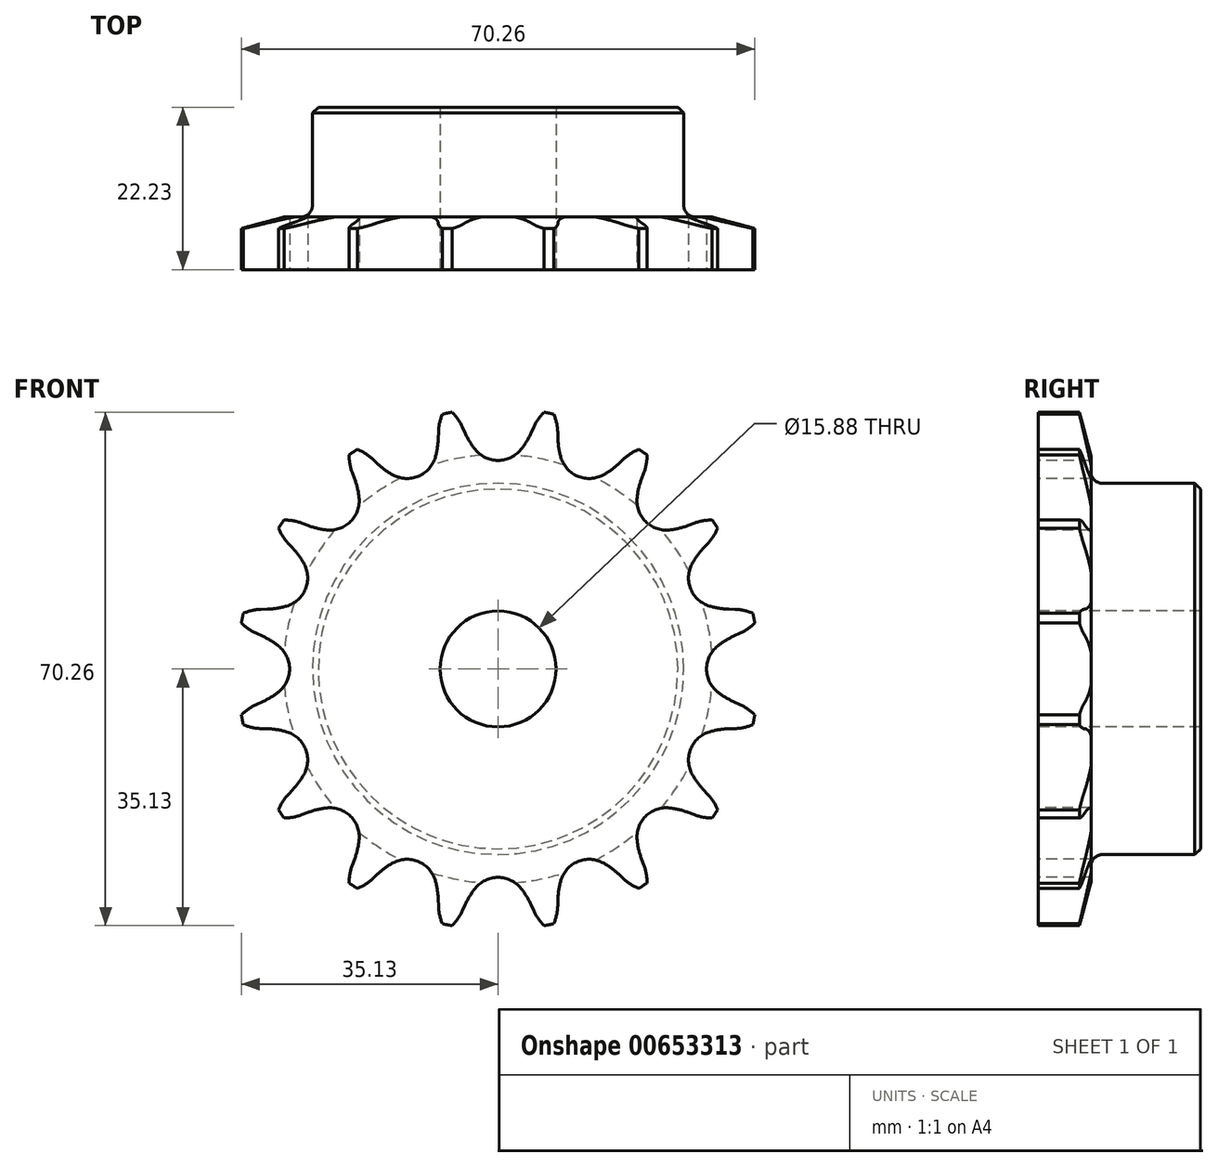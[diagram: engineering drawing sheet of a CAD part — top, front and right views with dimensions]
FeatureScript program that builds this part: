
annotation { "Feature Type Name" : "Feature", "Feature Type Description" : "" }
export const myFeature = defineFeature(function(context is Context, id is Id, definition is map)
    precondition{}
    {
        {
            var Q0;
            Q0=qCreatedBy(makeId("Right.planeOp"),FACE);
            var sketch = newSketch(context, id + "F0", { "sketchPlane" : qUnion([Q0])});
            skLineSegment(sketch, "E0", {"start": v(0, 0) * mm, "end": v(22.22, 0) * mm, "construction": true});
            skLineSegment(sketch, "E1", {"start": v(0, 35.69) * mm, "end": v(7.21, 35.69) * mm});
            skLineSegment(sketch, "E2", {"start": v(7.21, 35.69) * mm, "end": v(7.21, 25.4) * mm});
            skLineSegment(sketch, "E3", {"start": v(7.21, 25.4) * mm, "end": v(22.23, 25.4) * mm});
            skLineSegment(sketch, "E4", {"start": v(22.22, 25.4) * mm, "end": v(22.22, 7.94) * mm});
            skLineSegment(sketch, "E5", {"start": v(22.23, 7.94) * mm, "end": v(0, 7.94) * mm});
            skLineSegment(sketch, "E6", {"start": v(0, 7.94) * mm, "end": v(0, 35.69) * mm});
            skLineSegment(sketch, "E7.0.MirrorCS", {"start": v(0, -35.69) * mm, "end": v(7.21, -35.69) * mm});
            skLineSegment(sketch, "E7.1.MirrorCS", {"start": v(7.21, -35.69) * mm, "end": v(7.21, -25.4) * mm});
            skLineSegment(sketch, "E7.2.MirrorCS", {"start": v(22.23, -7.94) * mm, "end": v(0, -7.94) * mm});
            skLineSegment(sketch, "E7.3.MirrorCS", {"start": v(22.23, -25.4) * mm, "end": v(22.23, -7.94) * mm});
            skLineSegment(sketch, "E7.4.MirrorCS", {"start": v(7.21, -25.4) * mm, "end": v(22.23, -25.4) * mm});
            skLineSegment(sketch, "E7.5.MirrorCS", {"start": v(0, -7.94) * mm, "end": v(0, -35.69) * mm});
            skSolve(sketch);
        }
        {
            var Q0;
            Q0=makeQuery(id+"F0.imprint","IMPRINT",FACE,{"disambiguationData":[TD([[makeQuery(id+"F0.imprint","IMPRINT",EDGE,{"derivedFrom":sQuery(id+"F0.wireOp",EDGE,"E1")}),-1.0]])]});
            var Q1;
            Q1=sQuery(id+"F0.wireOp",EDGE,"E0");
            revolve(context, id + "F1", {"entities" : qUnion([Q0]), "axis" : qUnion([Q1]), "revolveType" : RevolveType.FULL});
        }
        {
            var Q0;
            Q0=makeQuery(id+"F1.opRevolve","SWEPT_EDGE",EDGE,{"disambiguationData":[OSD([sQuery(id+"F0.wireOp",EDGE,"E1"),sQuery(id+"F0.wireOp",EDGE,"E2")])]});
            chamfer(context, id + "F2", {"entities" : qUnion([Q0]), "chamferType" : ChamferType.TWO_OFFSETS, "width1" : 6.35 * mm, "oppositeDirection" : true, "width2" : 1.57 * mm, "tangentPropagation" : true});
        }
        {
            var Q0;
            Q0=makeQuery(id+"F1.opRevolve","SWEPT_FACE",FACE,{"disambiguationData":[OSD([sQuery(id+"F0.wireOp",EDGE,"E6")])]});
            var sketch = newSketch(context, id + "F3", { "sketchPlane" : qUnion([Q0])});
            skCircle(sketch, "E8", {"center": v(0, 0) * mm, "radius": 32.55 * mm, "construction": true});
            skLineSegment(sketch, "E9", {"start": v(0, 0) * mm, "end": v(0, 32.55) * mm, "construction": true});
            skLineSegment(sketch, "E10", {"start": v(0, 32.55) * mm, "end": v(25.8, 32.55) * mm, "construction": true});
            skPoint(sketch, "E11", {"position": v(-10.88, 30.38) * mm});
            skPoint(sketch, "E12", {"position": v(4.95, 36.52) * mm});
            skLineSegment(sketch, "E13", {"start": v(0, 32.55) * mm, "end": v(4.95, 36.52) * mm, "construction": true});
            skLineSegment(sketch, "E14", {"start": v(4.95, 36.52) * mm, "end": v(-4.5, 32.26) * mm, "construction": true});
            skLineSegment(sketch, "E15", {"start": v(-4.5, 32.26) * mm, "end": v(-4.88, 33.1) * mm});
            skLineSegment(sketch, "E16", {"start": v(0, 0) * mm, "end": v(-7.12, 35.8) * mm, "construction": true});
            skArc(sketch, "E17", {"start": v(-7.12, 35.8) * mm, "mid": v(-15.95, 26.17) * mm, "end": v(-4.88, 33.1) * mm, "construction": true});
            skArc(sketch, "E18", {"start": v(-4.88, 33.1) * mm, "mid": v(-5.81, 34.6) * mm, "end": v(-7.12, 35.8) * mm});
            skArc(sketch, "E19", {"start": v(-3.14, 30.03) * mm, "mid": v(13.78, 41.93) * mm, "end": v(-4.5, 32.26) * mm, "construction": true});
            skArc(sketch, "E20", {"start": v(-4.5, 32.26) * mm, "mid": v(-3.89, 31.1) * mm, "end": v(-3.14, 30.03) * mm});
            skLineSegment(sketch, "E21", {"start": v(4.4, 12.5) * mm, "end": v(-4.88, 33.1) * mm, "construction": true});
            skArc(sketch, "E22.0.MirrorCS", {"start": v(4.5, 32.26) * mm, "mid": v(3.89, 31.1) * mm, "end": v(3.14, 30.03) * mm});
            skLineSegment(sketch, "E23.0.MirrorCS", {"start": v(4.5, 32.26) * mm, "end": v(4.88, 33.1) * mm});
            skArc(sketch, "E24.0.MirrorCS", {"start": v(4.88, 33.1) * mm, "mid": v(5.81, 34.6) * mm, "end": v(7.12, 35.8) * mm});
            skArc(sketch, "E25", {"start": v(-3.14, 30.03) * mm, "mid": v(0, 28.53) * mm, "end": v(3.14, 30.03) * mm});
            skArc(sketch, "E26", {"start": v(3.14, 30.03) * mm, "mid": v(0, 36.57) * mm, "end": v(-3.14, 30.03) * mm, "construction": true});
            skArc(sketch, "E27.1.0", {"start": v(-17.17, 28.7) * mm, "mid": v(-18.61, 29.74) * mm, "end": v(-20.28, 30.34) * mm});
            skLineSegment(sketch, "E27.1.1", {"start": v(-16.5, 28.08) * mm, "end": v(-17.17, 28.7) * mm});
            skArc(sketch, "E27.1.2", {"start": v(-16.5, 28.08) * mm, "mid": v(-15.5, 27.25) * mm, "end": v(-14.39, 26.55) * mm});
            skArc(sketch, "E27.1.3", {"start": v(-14.39, 26.55) * mm, "mid": v(-10.92, 26.36) * mm, "end": v(-8.6, 28.95) * mm});
            skArc(sketch, "E27.1.4", {"start": v(-8.19, 31.53) * mm, "mid": v(-8.3, 30.22) * mm, "end": v(-8.6, 28.95) * mm});
            skLineSegment(sketch, "E27.1.5", {"start": v(-8.19, 31.53) * mm, "end": v(-8.16, 32.44) * mm});
            skArc(sketch, "E27.1.6", {"start": v(-8.16, 32.44) * mm, "mid": v(-7.87, 34.19) * mm, "end": v(-7.12, 35.8) * mm});
            skArc(sketch, "E27.2.0", {"start": v(-26.85, 19.95) * mm, "mid": v(-28.57, 20.35) * mm, "end": v(-30.34, 20.28) * mm});
            skLineSegment(sketch, "E27.2.1", {"start": v(-26, 19.63) * mm, "end": v(-26.85, 19.95) * mm});
            skArc(sketch, "E27.2.2", {"start": v(-26, 19.63) * mm, "mid": v(-24.74, 19.24) * mm, "end": v(-23.45, 19.02) * mm});
            skArc(sketch, "E27.2.3", {"start": v(-23.45, 19.02) * mm, "mid": v(-20.17, 20.17) * mm, "end": v(-19.02, 23.45) * mm});
            skArc(sketch, "E27.2.4", {"start": v(-19.63, 26) * mm, "mid": v(-19.24, 24.74) * mm, "end": v(-19.02, 23.45) * mm});
            skLineSegment(sketch, "E27.2.5", {"start": v(-19.63, 26) * mm, "end": v(-19.95, 26.85) * mm});
            skArc(sketch, "E27.2.6", {"start": v(-19.95, 26.85) * mm, "mid": v(-20.35, 28.57) * mm, "end": v(-20.28, 30.34) * mm});
            skArc(sketch, "E27.3.0", {"start": v(-32.44, 8.16) * mm, "mid": v(-34.19, 7.87) * mm, "end": v(-35.8, 7.12) * mm});
            skLineSegment(sketch, "E27.3.1", {"start": v(-31.53, 8.19) * mm, "end": v(-32.44, 8.16) * mm});
            skArc(sketch, "E27.3.2", {"start": v(-31.53, 8.19) * mm, "mid": v(-30.22, 8.3) * mm, "end": v(-28.95, 8.6) * mm});
            skArc(sketch, "E27.3.3", {"start": v(-28.95, 8.6) * mm, "mid": v(-26.36, 10.92) * mm, "end": v(-26.55, 14.39) * mm});
            skArc(sketch, "E27.3.4", {"start": v(-28.08, 16.5) * mm, "mid": v(-27.25, 15.5) * mm, "end": v(-26.55, 14.39) * mm});
            skLineSegment(sketch, "E27.3.5", {"start": v(-28.08, 16.5) * mm, "end": v(-28.7, 17.17) * mm});
            skArc(sketch, "E27.3.6", {"start": v(-28.7, 17.17) * mm, "mid": v(-29.74, 18.61) * mm, "end": v(-30.34, 20.28) * mm});
            skArc(sketch, "E27.4.0", {"start": v(-33.1, -4.88) * mm, "mid": v(-34.6, -5.81) * mm, "end": v(-35.8, -7.12) * mm});
            skLineSegment(sketch, "E27.4.1", {"start": v(-32.26, -4.5) * mm, "end": v(-33.1, -4.88) * mm});
            skArc(sketch, "E27.4.2", {"start": v(-32.26, -4.5) * mm, "mid": v(-31.1, -3.89) * mm, "end": v(-30.03, -3.14) * mm});
            skArc(sketch, "E27.4.3", {"start": v(-30.03, -3.14) * mm, "mid": v(-28.53, 0) * mm, "end": v(-30.03, 3.14) * mm});
            skArc(sketch, "E27.4.4", {"start": v(-32.26, 4.5) * mm, "mid": v(-31.1, 3.89) * mm, "end": v(-30.03, 3.14) * mm});
            skLineSegment(sketch, "E27.4.5", {"start": v(-32.26, 4.5) * mm, "end": v(-33.1, 4.88) * mm});
            skArc(sketch, "E27.4.6", {"start": v(-33.1, 4.88) * mm, "mid": v(-34.6, 5.81) * mm, "end": v(-35.8, 7.12) * mm});
            skArc(sketch, "E27.5.0", {"start": v(-28.7, -17.17) * mm, "mid": v(-29.74, -18.61) * mm, "end": v(-30.34, -20.28) * mm});
            skLineSegment(sketch, "E27.5.1", {"start": v(-28.08, -16.5) * mm, "end": v(-28.7, -17.17) * mm});
            skArc(sketch, "E27.5.2", {"start": v(-28.08, -16.5) * mm, "mid": v(-27.25, -15.5) * mm, "end": v(-26.55, -14.39) * mm});
            skArc(sketch, "E27.5.3", {"start": v(-26.55, -14.39) * mm, "mid": v(-26.36, -10.92) * mm, "end": v(-28.95, -8.6) * mm});
            skArc(sketch, "E27.5.4", {"start": v(-31.53, -8.19) * mm, "mid": v(-30.22, -8.3) * mm, "end": v(-28.95, -8.6) * mm});
            skLineSegment(sketch, "E27.5.5", {"start": v(-31.53, -8.19) * mm, "end": v(-32.44, -8.16) * mm});
            skArc(sketch, "E27.5.6", {"start": v(-32.44, -8.16) * mm, "mid": v(-34.19, -7.87) * mm, "end": v(-35.8, -7.12) * mm});
            skArc(sketch, "E27.6.0", {"start": v(-19.95, -26.85) * mm, "mid": v(-20.35, -28.57) * mm, "end": v(-20.28, -30.34) * mm});
            skLineSegment(sketch, "E27.6.1", {"start": v(-19.63, -26) * mm, "end": v(-19.95, -26.85) * mm});
            skArc(sketch, "E27.6.2", {"start": v(-19.63, -26) * mm, "mid": v(-19.24, -24.74) * mm, "end": v(-19.02, -23.45) * mm});
            skArc(sketch, "E27.6.3", {"start": v(-19.02, -23.45) * mm, "mid": v(-20.17, -20.17) * mm, "end": v(-23.45, -19.02) * mm});
            skArc(sketch, "E27.6.4", {"start": v(-26, -19.63) * mm, "mid": v(-24.74, -19.24) * mm, "end": v(-23.45, -19.02) * mm});
            skLineSegment(sketch, "E27.6.5", {"start": v(-26, -19.63) * mm, "end": v(-26.85, -19.95) * mm});
            skArc(sketch, "E27.6.6", {"start": v(-26.85, -19.95) * mm, "mid": v(-28.57, -20.35) * mm, "end": v(-30.34, -20.28) * mm});
            skArc(sketch, "E27.7.0", {"start": v(-8.16, -32.44) * mm, "mid": v(-7.87, -34.19) * mm, "end": v(-7.12, -35.8) * mm});
            skLineSegment(sketch, "E27.7.1", {"start": v(-8.19, -31.53) * mm, "end": v(-8.16, -32.44) * mm});
            skArc(sketch, "E27.7.2", {"start": v(-8.19, -31.53) * mm, "mid": v(-8.3, -30.22) * mm, "end": v(-8.6, -28.95) * mm});
            skArc(sketch, "E27.7.3", {"start": v(-8.6, -28.95) * mm, "mid": v(-10.92, -26.36) * mm, "end": v(-14.39, -26.55) * mm});
            skArc(sketch, "E27.7.4", {"start": v(-16.5, -28.08) * mm, "mid": v(-15.5, -27.25) * mm, "end": v(-14.39, -26.55) * mm});
            skLineSegment(sketch, "E27.7.5", {"start": v(-16.5, -28.08) * mm, "end": v(-17.17, -28.7) * mm});
            skArc(sketch, "E27.7.6", {"start": v(-17.17, -28.7) * mm, "mid": v(-18.61, -29.74) * mm, "end": v(-20.28, -30.34) * mm});
            skArc(sketch, "E27.8.0", {"start": v(4.88, -33.1) * mm, "mid": v(5.81, -34.6) * mm, "end": v(7.12, -35.8) * mm});
            skLineSegment(sketch, "E27.8.1", {"start": v(4.5, -32.26) * mm, "end": v(4.88, -33.1) * mm});
            skArc(sketch, "E27.8.2", {"start": v(4.5, -32.26) * mm, "mid": v(3.89, -31.1) * mm, "end": v(3.14, -30.03) * mm});
            skArc(sketch, "E27.8.3", {"start": v(3.14, -30.03) * mm, "mid": v(0, -28.53) * mm, "end": v(-3.14, -30.03) * mm});
            skArc(sketch, "E27.8.4", {"start": v(-4.5, -32.26) * mm, "mid": v(-3.89, -31.1) * mm, "end": v(-3.14, -30.03) * mm});
            skLineSegment(sketch, "E27.8.5", {"start": v(-4.5, -32.26) * mm, "end": v(-4.88, -33.1) * mm});
            skArc(sketch, "E27.8.6", {"start": v(-4.88, -33.1) * mm, "mid": v(-5.81, -34.6) * mm, "end": v(-7.12, -35.8) * mm});
            skArc(sketch, "E27.9.0", {"start": v(17.17, -28.7) * mm, "mid": v(18.61, -29.74) * mm, "end": v(20.28, -30.34) * mm});
            skLineSegment(sketch, "E27.9.1", {"start": v(16.5, -28.08) * mm, "end": v(17.17, -28.7) * mm});
            skArc(sketch, "E27.9.2", {"start": v(16.5, -28.08) * mm, "mid": v(15.5, -27.25) * mm, "end": v(14.39, -26.55) * mm});
            skArc(sketch, "E27.9.3", {"start": v(14.39, -26.55) * mm, "mid": v(10.92, -26.36) * mm, "end": v(8.6, -28.95) * mm});
            skArc(sketch, "E27.9.4", {"start": v(8.19, -31.53) * mm, "mid": v(8.3, -30.22) * mm, "end": v(8.6, -28.95) * mm});
            skLineSegment(sketch, "E27.9.5", {"start": v(8.19, -31.53) * mm, "end": v(8.16, -32.44) * mm});
            skArc(sketch, "E27.9.6", {"start": v(8.16, -32.44) * mm, "mid": v(7.87, -34.19) * mm, "end": v(7.12, -35.8) * mm});
            skArc(sketch, "E27.10.0", {"start": v(26.85, -19.95) * mm, "mid": v(28.57, -20.35) * mm, "end": v(30.34, -20.28) * mm});
            skLineSegment(sketch, "E27.10.1", {"start": v(26, -19.63) * mm, "end": v(26.85, -19.95) * mm});
            skArc(sketch, "E27.10.2", {"start": v(26, -19.63) * mm, "mid": v(24.74, -19.24) * mm, "end": v(23.45, -19.02) * mm});
            skArc(sketch, "E27.10.3", {"start": v(23.45, -19.02) * mm, "mid": v(20.17, -20.17) * mm, "end": v(19.02, -23.45) * mm});
            skArc(sketch, "E27.10.4", {"start": v(19.63, -26) * mm, "mid": v(19.24, -24.74) * mm, "end": v(19.02, -23.45) * mm});
            skLineSegment(sketch, "E27.10.5", {"start": v(19.63, -26) * mm, "end": v(19.95, -26.85) * mm});
            skArc(sketch, "E27.10.6", {"start": v(19.95, -26.85) * mm, "mid": v(20.35, -28.57) * mm, "end": v(20.28, -30.34) * mm});
            skArc(sketch, "E27.11.0", {"start": v(32.44, -8.16) * mm, "mid": v(34.19, -7.87) * mm, "end": v(35.8, -7.12) * mm});
            skLineSegment(sketch, "E27.11.1", {"start": v(31.53, -8.19) * mm, "end": v(32.44, -8.16) * mm});
            skArc(sketch, "E27.11.2", {"start": v(31.53, -8.19) * mm, "mid": v(30.22, -8.3) * mm, "end": v(28.95, -8.6) * mm});
            skArc(sketch, "E27.11.3", {"start": v(28.95, -8.6) * mm, "mid": v(26.36, -10.92) * mm, "end": v(26.55, -14.39) * mm});
            skArc(sketch, "E27.11.4", {"start": v(28.08, -16.5) * mm, "mid": v(27.25, -15.5) * mm, "end": v(26.55, -14.39) * mm});
            skLineSegment(sketch, "E27.11.5", {"start": v(28.08, -16.5) * mm, "end": v(28.7, -17.17) * mm});
            skArc(sketch, "E27.11.6", {"start": v(28.7, -17.17) * mm, "mid": v(29.74, -18.61) * mm, "end": v(30.34, -20.28) * mm});
            skArc(sketch, "E27.12.0", {"start": v(33.1, 4.88) * mm, "mid": v(34.6, 5.81) * mm, "end": v(35.8, 7.12) * mm});
            skLineSegment(sketch, "E27.12.1", {"start": v(32.26, 4.5) * mm, "end": v(33.1, 4.88) * mm});
            skArc(sketch, "E27.12.2", {"start": v(32.26, 4.5) * mm, "mid": v(31.1, 3.89) * mm, "end": v(30.03, 3.14) * mm});
            skArc(sketch, "E27.12.3", {"start": v(30.03, 3.14) * mm, "mid": v(28.53, 0) * mm, "end": v(30.03, -3.14) * mm});
            skArc(sketch, "E27.12.4", {"start": v(32.26, -4.5) * mm, "mid": v(31.1, -3.89) * mm, "end": v(30.03, -3.14) * mm});
            skLineSegment(sketch, "E27.12.5", {"start": v(32.26, -4.5) * mm, "end": v(33.1, -4.88) * mm});
            skArc(sketch, "E27.12.6", {"start": v(33.1, -4.88) * mm, "mid": v(34.6, -5.81) * mm, "end": v(35.8, -7.12) * mm});
            skArc(sketch, "E27.13.0", {"start": v(28.7, 17.17) * mm, "mid": v(29.74, 18.61) * mm, "end": v(30.34, 20.28) * mm});
            skLineSegment(sketch, "E27.13.1", {"start": v(28.08, 16.5) * mm, "end": v(28.7, 17.17) * mm});
            skArc(sketch, "E27.13.2", {"start": v(28.08, 16.5) * mm, "mid": v(27.25, 15.5) * mm, "end": v(26.55, 14.39) * mm});
            skArc(sketch, "E27.13.3", {"start": v(26.55, 14.39) * mm, "mid": v(26.36, 10.92) * mm, "end": v(28.95, 8.6) * mm});
            skArc(sketch, "E27.13.4", {"start": v(31.53, 8.19) * mm, "mid": v(30.22, 8.3) * mm, "end": v(28.95, 8.6) * mm});
            skLineSegment(sketch, "E27.13.5", {"start": v(31.53, 8.19) * mm, "end": v(32.44, 8.16) * mm});
            skArc(sketch, "E27.13.6", {"start": v(32.44, 8.16) * mm, "mid": v(34.19, 7.87) * mm, "end": v(35.8, 7.12) * mm});
            skArc(sketch, "E27.14.0", {"start": v(19.95, 26.85) * mm, "mid": v(20.35, 28.57) * mm, "end": v(20.28, 30.34) * mm});
            skLineSegment(sketch, "E27.14.1", {"start": v(19.63, 26) * mm, "end": v(19.95, 26.85) * mm});
            skArc(sketch, "E27.14.2", {"start": v(19.63, 26) * mm, "mid": v(19.24, 24.74) * mm, "end": v(19.02, 23.45) * mm});
            skArc(sketch, "E27.14.3", {"start": v(19.02, 23.45) * mm, "mid": v(20.17, 20.17) * mm, "end": v(23.45, 19.02) * mm});
            skArc(sketch, "E27.14.4", {"start": v(26, 19.63) * mm, "mid": v(24.74, 19.24) * mm, "end": v(23.45, 19.02) * mm});
            skLineSegment(sketch, "E27.14.5", {"start": v(26, 19.63) * mm, "end": v(26.85, 19.95) * mm});
            skArc(sketch, "E27.14.6", {"start": v(26.85, 19.95) * mm, "mid": v(28.57, 20.35) * mm, "end": v(30.34, 20.28) * mm});
            skArc(sketch, "E27.15.0", {"start": v(8.16, 32.44) * mm, "mid": v(7.87, 34.19) * mm, "end": v(7.12, 35.8) * mm});
            skLineSegment(sketch, "E27.15.1", {"start": v(8.19, 31.53) * mm, "end": v(8.16, 32.44) * mm});
            skArc(sketch, "E27.15.2", {"start": v(8.19, 31.53) * mm, "mid": v(8.3, 30.22) * mm, "end": v(8.6, 28.95) * mm});
            skArc(sketch, "E27.15.3", {"start": v(8.6, 28.95) * mm, "mid": v(10.92, 26.36) * mm, "end": v(14.39, 26.55) * mm});
            skArc(sketch, "E27.15.4", {"start": v(16.5, 28.08) * mm, "mid": v(15.5, 27.25) * mm, "end": v(14.39, 26.55) * mm});
            skLineSegment(sketch, "E27.15.5", {"start": v(16.5, 28.08) * mm, "end": v(17.17, 28.7) * mm});
            skArc(sketch, "E27.15.6", {"start": v(17.17, 28.7) * mm, "mid": v(18.61, 29.74) * mm, "end": v(20.28, 30.34) * mm});
            skSolve(sketch);
        }
        {
            var Q0;
            Q0=qSketchRegion(id+"F3",true);
            extrude(context, id + "F4", {"entities" : qUnion([Q0]), "operationType" : NewBodyOperationType.INTERSECT, "endBound" : BoundingType.THROUGH_ALL, "oppositeDirection" : true, "depth" : 25.4 * mm});
        }
        {
            var Q0;
            Q0=makeQuery(id+"F1.opRevolve","SWEPT_EDGE",EDGE,{"disambiguationData":[OSD([sQuery(id+"F0.wireOp",EDGE,"E2"),sQuery(id+"F0.wireOp",EDGE,"E3")])]});
            fillet(context, id + "F5", {"entities" : qUnion([Q0]), "radius" : 1.59 * mm, "tangentPropagation" : true, "allowEdgeOverflow" : false});
        }
        {
            var Q0;
            Q0=makeQuery(id+"F1.opRevolve","SWEPT_EDGE",EDGE,{"disambiguationData":[OSD([sQuery(id+"F0.wireOp",EDGE,"E3"),sQuery(id+"F0.wireOp",EDGE,"E4")])]});
            chamfer(context, id + "F6", {"entities" : qUnion([Q0]), "width" : 0.8 * mm, "tangentPropagation" : true});
        }
    });
